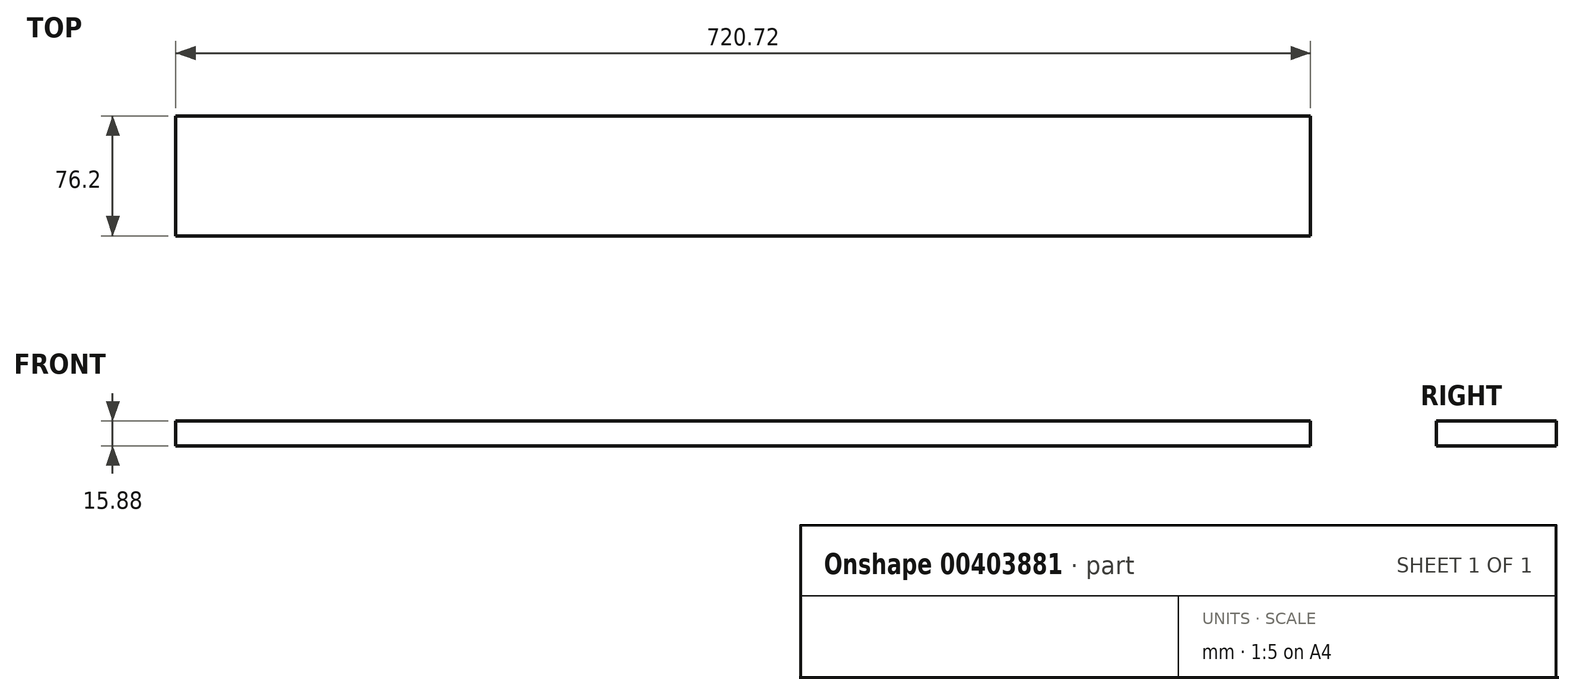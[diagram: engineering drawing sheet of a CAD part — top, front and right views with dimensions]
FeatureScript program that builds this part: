
annotation { "Feature Type Name" : "Feature", "Feature Type Description" : "" }
export const myFeature = defineFeature(function(context is Context, id is Id, definition is map)
    precondition{}
    {
        {
            var Q0;
            Q0=qCreatedBy(makeId("Top.planeOp"),FACE);
            var sketch = newSketch(context, id + "F0", { "sketchPlane" : qUnion([Q0])});
            skLineSegment(sketch, "E0.bottom", {"start": v(360.36, -38.1) * mm, "end": v(-360.36, -38.1) * mm});
            skLineSegment(sketch, "E0.top", {"start": v(360.36, 38.1) * mm, "end": v(-360.36, 38.1) * mm});
            skLineSegment(sketch, "E0.left", {"start": v(360.36, -38.1) * mm, "end": v(360.36, 38.1) * mm});
            skLineSegment(sketch, "E0.right", {"start": v(-360.36, -38.1) * mm, "end": v(-360.36, 38.1) * mm});
            skPoint(sketch, "E0.middle", {"position": v(0, 0) * mm});
            skSolve(sketch);
        }
        {
            var Q0;
            Q0 = qSketchRegion(id + "F0", true);
            extrude(context, id + "F1", {"entities" : qUnion([Q0]), "oppositeDirection" : true, "depth" : 15.88 * mm});
        }
    });
